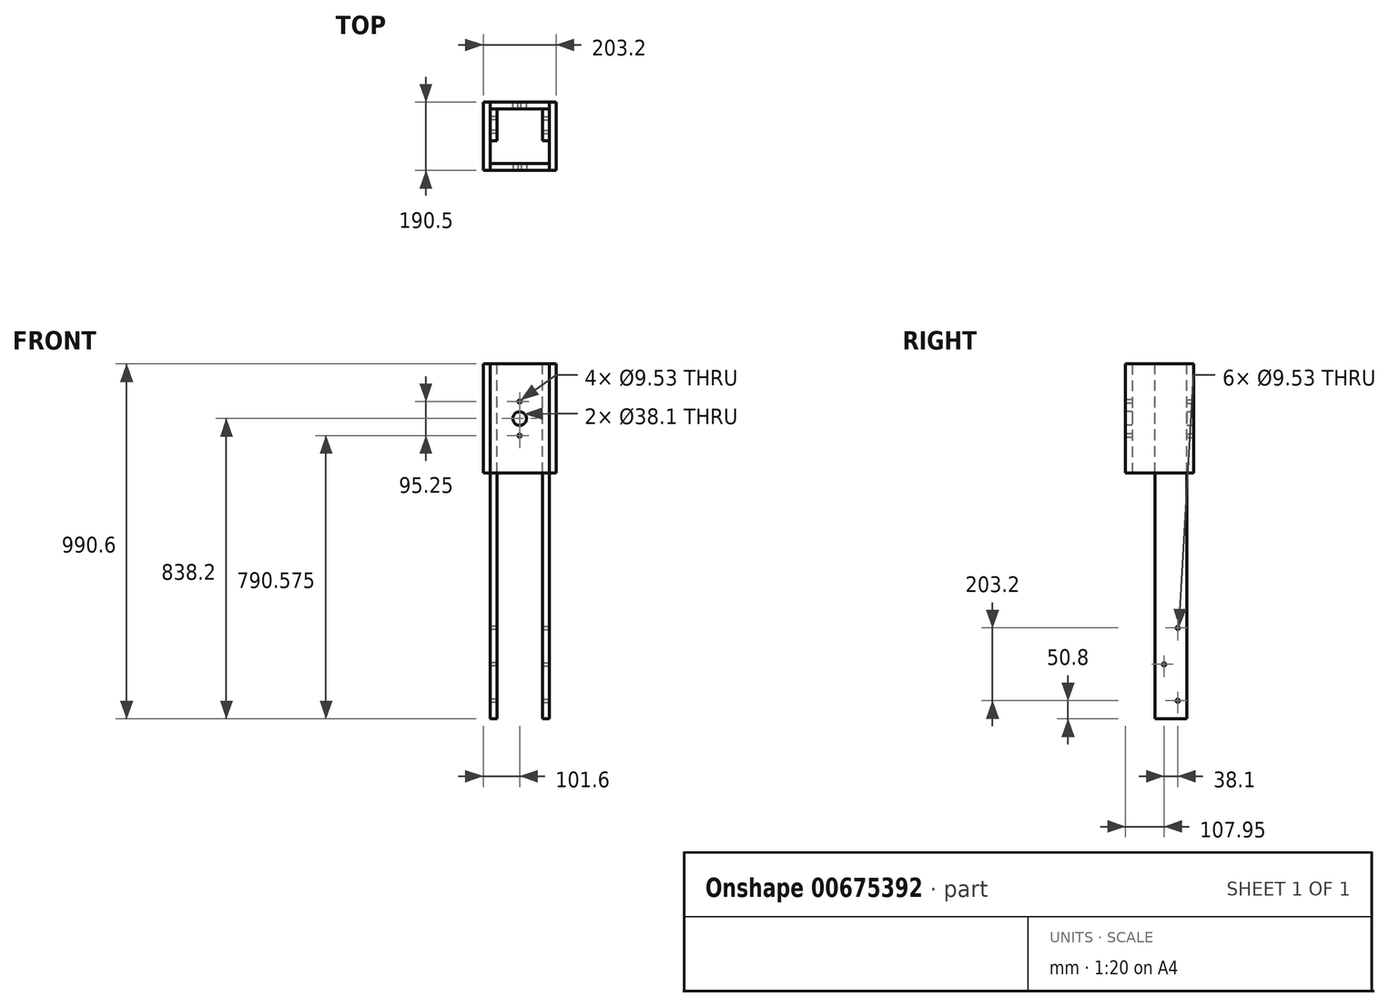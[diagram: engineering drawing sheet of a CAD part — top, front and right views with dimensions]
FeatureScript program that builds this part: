
annotation { "Feature Type Name" : "Feature", "Feature Type Description" : "" }
export const myFeature = defineFeature(function(context is Context, id is Id, definition is map)
    precondition{}
    {
        {
            var Q0;
            Q0=qCreatedBy(makeId("Top.planeOp"),FACE);
            var sketch = newSketch(context, id + "F0", { "sketchPlane" : qUnion([Q0])});
            skLineSegment(sketch, "E0.bottom", {"start": v(82.55, -95.25) * mm, "end": v(101.6, -95.25) * mm});
            skLineSegment(sketch, "E0.top", {"start": v(82.55, 95.25) * mm, "end": v(101.6, 95.25) * mm});
            skLineSegment(sketch, "E0.left", {"start": v(82.55, -95.25) * mm, "end": v(82.55, 95.25) * mm});
            skLineSegment(sketch, "E0.right", {"start": v(101.6, -95.25) * mm, "end": v(101.6, 95.25) * mm});
            skLineSegment(sketch, "E1.bottom", {"start": v(-101.6, -95.25) * mm, "end": v(-82.55, -95.25) * mm});
            skLineSegment(sketch, "E1.top", {"start": v(-101.6, 95.25) * mm, "end": v(-82.55, 95.25) * mm});
            skLineSegment(sketch, "E1.left", {"start": v(-101.6, -95.25) * mm, "end": v(-101.6, 95.25) * mm});
            skLineSegment(sketch, "E1.right", {"start": v(-82.55, -95.25) * mm, "end": v(-82.55, 95.25) * mm});
            skSolve(sketch);
        }
        {
            var Q0;
            Q0 = qSketchRegion(id + "F0", true);
            extrude(context, id + "F1", {"entities" : qUnion([Q0]), "depth" : 304.8 * mm, "offsetDistance" : 25.4 * mm});
        }
        {
            var Q0;
            Q0=qCreatedBy(makeId("Top.planeOp"),FACE);
            var sketch = newSketch(context, id + "F2", { "sketchPlane" : qUnion([Q0])});
            skLineSegment(sketch, "E2.bottom", {"start": v(-82.55, -95.25) * mm, "end": v(82.55, -95.25) * mm});
            skLineSegment(sketch, "E2.top", {"start": v(-82.55, -76.2) * mm, "end": v(82.55, -76.2) * mm});
            skLineSegment(sketch, "E2.left", {"start": v(-82.55, -95.25) * mm, "end": v(-82.55, -76.2) * mm});
            skLineSegment(sketch, "E2.right", {"start": v(82.55, -95.25) * mm, "end": v(82.55, -76.2) * mm});
            skLineSegment(sketch, "E3.bottom", {"start": v(-82.55, 95.25) * mm, "end": v(82.55, 95.25) * mm});
            skLineSegment(sketch, "E3.top", {"start": v(-82.55, 76.2) * mm, "end": v(82.55, 76.2) * mm});
            skLineSegment(sketch, "E3.left", {"start": v(-82.55, 95.25) * mm, "end": v(-82.55, 76.2) * mm});
            skLineSegment(sketch, "E3.right", {"start": v(82.55, 95.25) * mm, "end": v(82.55, 76.2) * mm});
            skSolve(sketch);
        }
        {
            var Q0;
            Q0 = qSketchRegion(id + "F2", true);
            extrude(context, id + "F3", {"entities" : qUnion([Q0]), "depth" : 304.8 * mm, "offsetDistance" : 25.4 * mm});
        }
        {
            var Q0;
            Q0=makeQuery(id+"F3.opExtrude","SWEPT_FACE",FACE,{"disambiguationData":[OSD([sQuery(id+"F2.wireOp",EDGE,"E2.bottom")])]});
            var sketch = newSketch(context, id + "F4", { "sketchPlane" : qUnion([Q0])});
            skCircle(sketch, "E4", {"center": v(0, 200.03) * mm, "radius": 4.76 * mm});
            skCircle(sketch, "E5", {"center": v(0, 152.4) * mm, "radius": 19.05 * mm});
            skCircle(sketch, "E6", {"center": v(0, 104.78) * mm, "radius": 4.76 * mm});
            skSolve(sketch);
        }
        {
            var Q0;
            Q0 = qSketchRegion(id + "F4", true);
            extrude(context, id + "F5", {"entities" : qUnion([Q0]), "operationType" : NewBodyOperationType.REMOVE, "oppositeDirection" : true, "depth" : 25.4 * mm, "offsetDistance" : 25.4 * mm});
        }
        {
            var Q0;
            Q0=makeQuery(id+"F3.opExtrude","SWEPT_FACE",FACE,{"disambiguationData":[OSD([sQuery(id+"F2.wireOp",EDGE,"E3.bottom")])]});
            var sketch = newSketch(context, id + "F6", { "sketchPlane" : qUnion([Q0])});
            skCircle(sketch, "E7", {"center": v(0, 104.78) * mm, "radius": 4.76 * mm});
            skCircle(sketch, "E8", {"center": v(0, 152.4) * mm, "radius": 19.05 * mm});
            skCircle(sketch, "E9", {"center": v(0, 200.03) * mm, "radius": 4.76 * mm});
            skSolve(sketch);
        }
        {
            var Q0;
            Q0 = qSketchRegion(id + "F6", true);
            extrude(context, id + "F7", {"entities" : qUnion([Q0]), "operationType" : NewBodyOperationType.REMOVE, "oppositeDirection" : true, "depth" : 25.4 * mm, "offsetDistance" : 25.4 * mm});
        }
        {
            var Q0;
            Q0=makeQuery(id+"F3.opExtrude","CAP_FACE",FACE,{"disambiguationData":[OSD([sQuery(id+"F2.wireOp",EDGE,"E2.bottom"),sQuery(id+"F2.wireOp",EDGE,"E2.top"),sQuery(id+"F2.wireOp",EDGE,"E2.left"),sQuery(id+"F2.wireOp",EDGE,"E2.right")])],"isStart":false});
            var sketch = newSketch(context, id + "F8", { "sketchPlane" : qUnion([Q0])});
            skLineSegment(sketch, "E10.bottom", {"start": v(-82.55, 76.2) * mm, "end": v(-63.5, 76.2) * mm});
            skLineSegment(sketch, "E10.top", {"start": v(-82.55, -12.7) * mm, "end": v(-63.5, -12.7) * mm});
            skLineSegment(sketch, "E10.left", {"start": v(-82.55, 76.2) * mm, "end": v(-82.55, -12.7) * mm});
            skLineSegment(sketch, "E10.right", {"start": v(-63.5, 76.2) * mm, "end": v(-63.5, -12.7) * mm});
            skLineSegment(sketch, "E11.bottom", {"start": v(82.55, 76.2) * mm, "end": v(63.5, 76.2) * mm});
            skLineSegment(sketch, "E11.top", {"start": v(82.55, -12.7) * mm, "end": v(63.5, -12.7) * mm});
            skLineSegment(sketch, "E11.left", {"start": v(82.55, 76.2) * mm, "end": v(82.55, -12.7) * mm});
            skLineSegment(sketch, "E11.right", {"start": v(63.5, 76.2) * mm, "end": v(63.5, -12.7) * mm});
            skSolve(sketch);
        }
        {
            var Q0;
            Q0 = qSketchRegion(id + "F8", true);
            extrude(context, id + "F9", {"entities" : qUnion([Q0]), "oppositeDirection" : true, "depth" : 990.6 * mm, "offsetDistance" : 25.4 * mm});
        }
        {
            var Q0;
            Q0=makeQuery(id+"F9.opExtrude","SWEPT_FACE",FACE,{"disambiguationData":[OSD([sQuery(id+"F8.wireOp",EDGE,"E11.left")])]});
            var sketch = newSketch(context, id + "F10", { "sketchPlane" : qUnion([Q0])});
            skCircle(sketch, "E12", {"center": v(50.8, -635) * mm, "radius": 4.76 * mm});
            skCircle(sketch, "E13", {"center": v(12.7, -533.4) * mm, "radius": 4.76 * mm});
            skCircle(sketch, "E14", {"center": v(50.8, -431.8) * mm, "radius": 4.76 * mm});
            skSolve(sketch);
        }
        {
            var Q0;
            Q0 = qSketchRegion(id + "F10", true);
            extrude(context, id + "F11", {"entities" : qUnion([Q0]), "operationType" : NewBodyOperationType.REMOVE, "oppositeDirection" : true, "depth" : 25.4 * mm, "offsetDistance" : 25.4 * mm});
        }
        {
            var Q0;
            Q0=makeQuery(id+"F9.opExtrude","SWEPT_FACE",FACE,{"disambiguationData":[OSD([sQuery(id+"F8.wireOp",EDGE,"E10.left")])]});
            var sketch = newSketch(context, id + "F12", { "sketchPlane" : qUnion([Q0])});
            skCircle(sketch, "E15", {"center": v(-50.8, -431.8) * mm, "radius": 4.76 * mm});
            skCircle(sketch, "E16", {"center": v(-50.8, -635) * mm, "radius": 4.76 * mm});
            skCircle(sketch, "E17", {"center": v(-12.7, -533.4) * mm, "radius": 4.76 * mm});
            skSolve(sketch);
        }
        {
            var Q0;
            Q0 = qSketchRegion(id + "F12", true);
            extrude(context, id + "F13", {"entities" : qUnion([Q0]), "operationType" : NewBodyOperationType.REMOVE, "oppositeDirection" : true, "depth" : 25.4 * mm, "offsetDistance" : 25.4 * mm});
        }
    });
